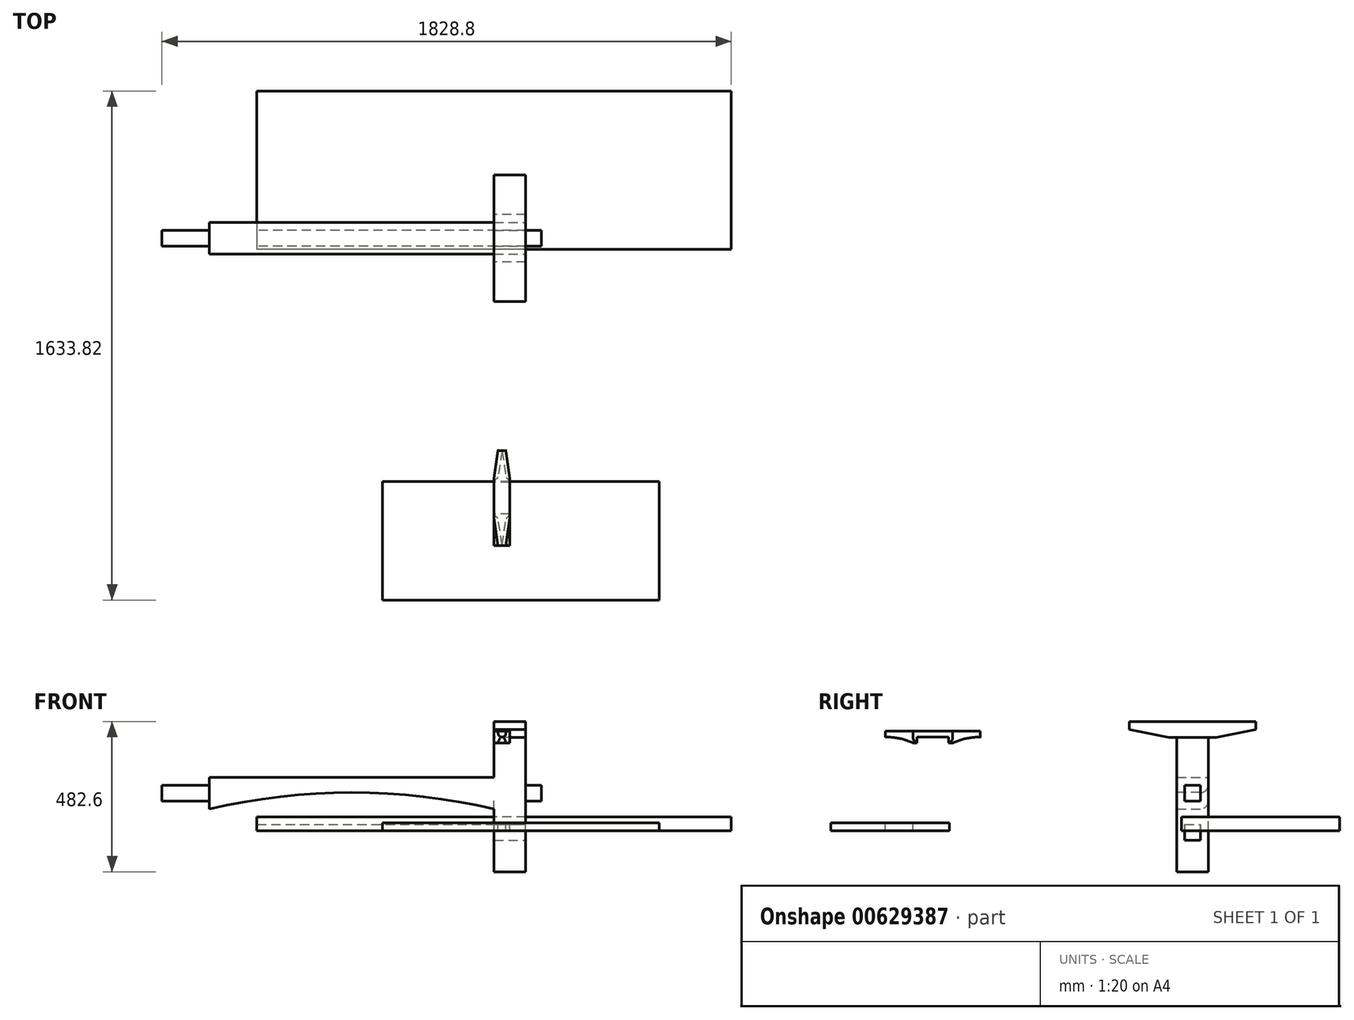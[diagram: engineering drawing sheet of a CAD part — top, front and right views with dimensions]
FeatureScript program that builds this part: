
annotation { "Feature Type Name" : "Feature", "Feature Type Description" : "" }
export const myFeature = defineFeature(function(context is Context, id is Id, definition is map)
    precondition{}
    {
        {
            var Q0;
            Q0=qCreatedBy(makeId("Top.planeOp"),FACE);
            var sketch = newSketch(context, id + "F0", { "sketchPlane" : qUnion([Q0])});
            skLineSegment(sketch, "E0.bottom", {"start": v(762, 260.88) * mm, "end": v(-762, 260.88) * mm});
            skLineSegment(sketch, "E0.top", {"start": v(762, -247.12) * mm, "end": v(-762, -247.12) * mm});
            skLineSegment(sketch, "E0.left", {"start": v(762, 260.88) * mm, "end": v(762, -247.12) * mm});
            skLineSegment(sketch, "E0.right", {"start": v(-762, 260.88) * mm, "end": v(-762, -247.12) * mm});
            skPoint(sketch, "E0.middle", {"position": v(0, 6.88) * mm});
            skSolve(sketch);
        }
        {
            var Q0;
            Q0=makeQuery(id+"F0.imprint","IMPRINT",FACE,{"disambiguationData":[TD([[makeQuery(id+"F0.imprint","IMPRINT",EDGE,{"derivedFrom":sQuery(id+"F0.wireOp",EDGE,"E0.bottom")}),1.0]])]});
            extrude(context, id + "F1", {"entities" : qUnion([Q0]), "depth" : 44.45 * mm, "offsetDistance" : 25.4 * mm});
        }
        {
            var Q0;
            Q0=qCreatedBy(makeId("Right.planeOp"),FACE);
            var sketch = newSketch(context, id + "F2", { "sketchPlane" : qUnion([Q0])});
            skLineSegment(sketch, "E1.bottom", {"start": v(-135.26, 299.84) * mm, "end": v(-287.66, 299.84) * mm});
            skLineSegment(sketch, "E1.top", {"start": v(-8.26, 350.64) * mm, "end": v(-414.66, 350.64) * mm});
            skLineSegment(sketch, "E1.left", {"start": v(-8.26, 325.24) * mm, "end": v(-8.26, 350.64) * mm});
            skLineSegment(sketch, "E1.right", {"start": v(-414.66, 325.24) * mm, "end": v(-414.66, 350.64) * mm});
            skPoint(sketch, "E1.middle", {"position": v(-211.46, 325.24) * mm});
            skLineSegment(sketch, "E2", {"start": v(-414.66, 325.24) * mm, "end": v(-287.66, 299.84) * mm});
            skLineSegment(sketch, "E3", {"start": v(-211.46, 459.59) * mm, "end": v(-211.46, 211.02) * mm, "construction": true});
            skPoint(sketch, "E3.startSnap0", {"position": v(-211.46, 350.64) * mm});
            skPoint(sketch, "E4.orphan", {"position": v(-414.66, 299.84) * mm});
            skLineSegment(sketch, "E5.MirrorCS", {"start": v(-8.26, 325.24) * mm, "end": v(-135.26, 299.84) * mm});
            skPoint(sketch, "E6.orphan", {"position": v(-8.26, 299.84) * mm});
            skSolve(sketch);
        }
        {
            var Q0;
            Q0=makeQuery(id+"F2.imprint","IMPRINT",FACE,{"disambiguationData":[TD([[makeQuery(id+"F2.imprint","IMPRINT",EDGE,{"derivedFrom":sQuery(id+"F2.wireOp",EDGE,"E1.bottom")}),-1.0]])]});
            extrude(context, id + "F3", {"entities" : qUnion([Q0]), "depth" : 101.6 * mm, "offsetDistance" : 25.4 * mm});
        }
        {
            var Q0;
            Q0=makeQuery(id+"F3.opExtrude","SWEPT_FACE",FACE,{"disambiguationData":[OSD([sQuery(id+"F2.wireOp",EDGE,"E1.bottom")])]});
            var sketch = newSketch(context, id + "F4", { "sketchPlane" : qUnion([Q0])});
            skLineSegment(sketch, "E7.bottom", {"start": v(0, 160.66) * mm, "end": v(101.6, 160.66) * mm});
            skLineSegment(sketch, "E7.top", {"start": v(0, 262.26) * mm, "end": v(101.6, 262.26) * mm});
            skLineSegment(sketch, "E7.left", {"start": v(0, 160.66) * mm, "end": v(0, 262.26) * mm});
            skLineSegment(sketch, "E7.right", {"start": v(101.6, 160.66) * mm, "end": v(101.6, 262.26) * mm});
            skPoint(sketch, "E7.middle", {"position": v(50.8, 211.46) * mm});
            skPoint(sketch, "E7.middle.positionSnap0", {"position": v(50.8, 135.26) * mm});
            skPoint(sketch, "E7.middle.positionSnap1", {"position": v(101.6, 211.46) * mm});
            skPoint(sketch, "E7.centerSnap0", {"position": v(50.8, 135.26) * mm});
            skPoint(sketch, "E7.centerSnap1", {"position": v(101.6, 211.46) * mm});
            skSolve(sketch);
        }
        {
            var Q0;
            Q0=makeQuery(id+"F4.imprint","IMPRINT",FACE,{"disambiguationData":[TD([[makeQuery(id+"F4.imprint","IMPRINT",EDGE,{"derivedFrom":sQuery(id+"F4.wireOp",EDGE,"E7.bottom")}),1.0]])]});
            extrude(context, id + "F5", {"entities" : qUnion([Q0]), "depth" : 431.8 * mm, "offsetDistance" : 25.4 * mm});
        }
        {
            var Q0;
            Q0=makeQuery(id+"F5.opExtrude","SWEPT_FACE",FACE,{"disambiguationData":[OSD([sQuery(id+"F4.wireOp",EDGE,"E7.left")])]});
            var sketch = newSketch(context, id + "F6", { "sketchPlane" : qUnion([Q0])});
            skLineSegment(sketch, "E8.bottom", {"start": v(262.26, 171.12) * mm, "end": v(160.66, 171.12) * mm});
            skLineSegment(sketch, "E8.top", {"start": v(262.26, 69.52) * mm, "end": v(160.66, 69.52) * mm});
            skLineSegment(sketch, "E8.left", {"start": v(262.26, 171.12) * mm, "end": v(262.26, 69.52) * mm});
            skLineSegment(sketch, "E8.right", {"start": v(160.66, 171.12) * mm, "end": v(160.66, 69.52) * mm});
            skPoint(sketch, "E8.middle", {"position": v(211.46, 120.32) * mm});
            skPoint(sketch, "E8.middle.positionSnap0", {"position": v(211.46, 299.84) * mm});
            skPoint(sketch, "E8.centerSnap0", {"position": v(211.46, 299.84) * mm});
            skSolve(sketch);
        }
        {
            var Q0;
            Q0=makeQuery(id+"F6.imprint","IMPRINT",FACE,{"disambiguationData":[TD([[makeQuery(id+"F6.imprint","IMPRINT",EDGE,{"derivedFrom":sQuery(id+"F6.wireOp",EDGE,"E8.bottom")}),1.0]])]});
            extrude(context, id + "F7", {"entities" : qUnion([Q0]), "depth" : 914.4 * mm, "offsetDistance" : 25.4 * mm});
        }
        {
            var Q0;
            Q0=makeQuery(id+"F7.opExtrude","CAP_FACE",FACE,{"disambiguationData":[OSD([sQuery(id+"F6.wireOp",EDGE,"E8.bottom"),sQuery(id+"F6.wireOp",EDGE,"E8.top"),sQuery(id+"F6.wireOp",EDGE,"E8.left"),sQuery(id+"F6.wireOp",EDGE,"E8.right")])],"isStart":true});
            var sketch = newSketch(context, id + "F8", { "sketchPlane" : qUnion([Q0])});
            skLineSegment(sketch, "E9.bottom", {"start": v(-186.06, 145.72) * mm, "end": v(-236.86, 145.72) * mm});
            skLineSegment(sketch, "E9.top", {"start": v(-186.06, 94.92) * mm, "end": v(-236.86, 94.92) * mm});
            skLineSegment(sketch, "E9.left", {"start": v(-186.06, 145.72) * mm, "end": v(-186.06, 94.92) * mm});
            skLineSegment(sketch, "E9.right", {"start": v(-236.86, 145.72) * mm, "end": v(-236.86, 94.92) * mm});
            skPoint(sketch, "E9.middle", {"position": v(-211.46, 120.32) * mm});
            skPoint(sketch, "E9.middle.positionSnap0", {"position": v(-262.26, 120.32) * mm});
            skPoint(sketch, "E9.middle.positionSnap1", {"position": v(-211.46, 171.12) * mm});
            skPoint(sketch, "E9.centerSnap0", {"position": v(-262.26, 120.32) * mm});
            skPoint(sketch, "E9.centerSnap1", {"position": v(-211.46, 171.12) * mm});
            skSolve(sketch);
        }
        {
            var Q0;
            Q0=makeQuery(id+"F8.imprint","IMPRINT",FACE,{"disambiguationData":[TD([[makeQuery(id+"F8.imprint","IMPRINT",EDGE,{"derivedFrom":sQuery(id+"F8.wireOp",EDGE,"E9.bottom")}),1.0]])]});
            extrude(context, id + "F9", {"entities" : qUnion([Q0]), "operationType" : NewBodyOperationType.ADD, "depth" : 152.4 * mm, "offsetDistance" : 25.4 * mm});
        }
        {
            var Q0;
            Q0=makeQuery(id+"F5.opExtrude","SWEPT_FACE",FACE,{"disambiguationData":[OSD([sQuery(id+"F4.wireOp",EDGE,"E7.right")])]});
            var sketch = newSketch(context, id + "F10", { "sketchPlane" : qUnion([Q0])});
            skLineSegment(sketch, "E10.bottom", {"start": v(-186.06, -30.36) * mm, "end": v(-236.86, -30.36) * mm});
            skLineSegment(sketch, "E10.top", {"start": v(-186.06, 20.44) * mm, "end": v(-236.86, 20.44) * mm});
            skLineSegment(sketch, "E10.left", {"start": v(-186.06, -30.36) * mm, "end": v(-186.06, 20.44) * mm});
            skLineSegment(sketch, "E10.right", {"start": v(-236.86, -30.36) * mm, "end": v(-236.86, 20.44) * mm});
            skPoint(sketch, "E10.middle", {"position": v(-211.46, -4.96) * mm});
            skPoint(sketch, "E10.middle.positionSnap0", {"position": v(-211.46, -131.96) * mm});
            skPoint(sketch, "E10.centerSnap0", {"position": v(-211.46, -131.96) * mm});
            skSolve(sketch);
        }
        {
            var Q0;
            Q0=makeQuery(id+"F10.imprint","IMPRINT",FACE,{"disambiguationData":[TD([[makeQuery(id+"F10.imprint","IMPRINT",EDGE,{"derivedFrom":sQuery(id+"F10.wireOp",EDGE,"E10.bottom")}),-1.0]])]});
            extrude(context, id + "F11", {"entities" : qUnion([Q0]), "operationType" : NewBodyOperationType.REMOVE, "endBound" : BoundingType.THROUGH_ALL, "oppositeDirection" : true, "depth" : 25.4 * mm, "offsetDistance" : 25.4 * mm});
        }
        {
            var Q0;
            Q0=makeQuery(id+"F7.opExtrude","CAP_FACE",FACE,{"disambiguationData":[OSD([sQuery(id+"F6.wireOp",EDGE,"E8.bottom"),sQuery(id+"F6.wireOp",EDGE,"E8.top"),sQuery(id+"F6.wireOp",EDGE,"E8.left"),sQuery(id+"F6.wireOp",EDGE,"E8.right")])],"isStart":false});
            var sketch = newSketch(context, id + "F12", { "sketchPlane" : qUnion([Q0])});
            skLineSegment(sketch, "E11.bottom", {"start": v(236.86, 145.72) * mm, "end": v(186.06, 145.72) * mm});
            skLineSegment(sketch, "E11.top", {"start": v(236.86, 94.92) * mm, "end": v(186.06, 94.92) * mm});
            skLineSegment(sketch, "E11.left", {"start": v(236.86, 145.72) * mm, "end": v(236.86, 94.92) * mm});
            skLineSegment(sketch, "E11.right", {"start": v(186.06, 145.72) * mm, "end": v(186.06, 94.92) * mm});
            skPoint(sketch, "E11.middle", {"position": v(211.46, 120.32) * mm});
            skPoint(sketch, "E11.middle.positionSnap0", {"position": v(262.26, 120.32) * mm});
            skPoint(sketch, "E11.middle.positionSnap1", {"position": v(211.46, 171.12) * mm});
            skPoint(sketch, "E11.centerSnap0", {"position": v(262.26, 120.32) * mm});
            skPoint(sketch, "E11.centerSnap1", {"position": v(211.46, 171.12) * mm});
            skSolve(sketch);
        }
        {
            var Q0;
            Q0=makeQuery(id+"F12.imprint","IMPRINT",FACE,{"disambiguationData":[TD([[makeQuery(id+"F12.imprint","IMPRINT",EDGE,{"derivedFrom":sQuery(id+"F12.wireOp",EDGE,"E11.bottom")}),1.0]])]});
            extrude(context, id + "F13", {"entities" : qUnion([Q0]), "operationType" : NewBodyOperationType.ADD, "depth" : 152.4 * mm, "offsetDistance" : 25.4 * mm});
        }
        {
            var Q0;
            Q0=qCreatedBy(makeId("Top.planeOp"),FACE);
            var sketch = newSketch(context, id + "F14", { "sketchPlane" : qUnion([Q0])});
            skLineSegment(sketch, "E12.bottom", {"start": v(530.86, -1372.94) * mm, "end": v(-358.14, -1372.94) * mm});
            skLineSegment(sketch, "E12.top", {"start": v(530.86, -991.94) * mm, "end": v(-358.14, -991.94) * mm});
            skLineSegment(sketch, "E12.left", {"start": v(530.86, -1372.94) * mm, "end": v(530.86, -991.94) * mm});
            skLineSegment(sketch, "E12.right", {"start": v(-358.14, -1372.94) * mm, "end": v(-358.14, -991.94) * mm});
            skPoint(sketch, "E12.middle", {"position": v(86.36, -1182.44) * mm});
            skSolve(sketch);
        }
        {
            var Q0;
            Q0=makeQuery(id+"F14.imprint","IMPRINT",FACE,{"disambiguationData":[TD([[makeQuery(id+"F14.imprint","IMPRINT",EDGE,{"derivedFrom":sQuery(id+"F14.wireOp",EDGE,"E12.bottom")}),-1.0]])]});
            extrude(context, id + "F15", {"entities" : qUnion([Q0]), "depth" : 25.4 * mm, "offsetDistance" : 25.4 * mm});
        }
        {
            var Q0;
            Q0=makeQuery(id+"F7.opExtrude","SWEPT_FACE",FACE,{"disambiguationData":[OSD([sQuery(id+"F6.wireOp",EDGE,"E8.left")])]});
            var sketch = newSketch(context, id + "F16", { "sketchPlane" : qUnion([Q0])});
            skArc(sketch, "E13", {"start": v(0, 69.52) * mm, "mid": v(-457.2, 122.3) * mm, "end": v(-914.4, 69.52) * mm});
            skSolve(sketch);
        }
        {
            var Q0;
            Q0=makeQuery(id+"F16.imprint","IMPRINT",FACE,{"disambiguationData":[TD([[makeQuery(id+"F16.imprint","IMPRINT",EDGE,{"derivedFrom":sQuery(id+"F16.wireOp",EDGE,"E13")}),1.0]])]});
            extrude(context, id + "F17", {"entities" : qUnion([Q0]), "operationType" : NewBodyOperationType.REMOVE, "endBound" : BoundingType.THROUGH_ALL, "oppositeDirection" : true, "depth" : 25.4 * mm, "offsetDistance" : 25.4 * mm});
        }
        {
            var Q0;
            Q0=qCreatedBy(makeId("Right.planeOp"),FACE);
            var sketch = newSketch(context, id + "F18", { "sketchPlane" : qUnion([Q0])});
            skLineSegment(sketch, "E14.bottom", {"start": v(-981.8, 281.46) * mm, "end": v(-994.5, 281.46) * mm});
            skLineSegment(sketch, "E14.top", {"start": v(-892.9, 319.56) * mm, "end": v(-1197.7, 319.56) * mm});
            skLineSegment(sketch, "E14.left", {"start": v(-892.9, 300.51) * mm, "end": v(-892.9, 319.56) * mm});
            skLineSegment(sketch, "E14.right", {"start": v(-1197.7, 300.51) * mm, "end": v(-1197.7, 319.56) * mm});
            skPoint(sketch, "E14.middle", {"position": v(-1045.3, 300.51) * mm});
            skPoint(sketch, "E15.orphan", {"position": v(-1197.7, 281.46) * mm});
            skLineSegment(sketch, "E16", {"start": v(-1045.3, 344.35) * mm, "end": v(-1045.3, 234.3) * mm, "construction": true});
            skPoint(sketch, "E17.orphan", {"position": v(-892.9, 281.46) * mm});
            skLineSegment(sketch, "E18.top", {"start": v(-994.5, 300.51) * mm, "end": v(-1096.1, 300.51) * mm});
            skLineSegment(sketch, "E18.left", {"start": v(-994.5, 281.46) * mm, "end": v(-994.5, 300.51) * mm});
            skLineSegment(sketch, "E18.right", {"start": v(-1096.1, 281.46) * mm, "end": v(-1096.1, 300.51) * mm});
            skPoint(sketch, "E18.middle", {"position": v(-1045.3, 281.46) * mm});
            skLineSegment(sketch, "E19.trimOffspring", {"start": v(-1096.1, 281.46) * mm, "end": v(-1108.8, 281.46) * mm});
            skArc(sketch, "E20", {"start": v(-1108.8, 281.46) * mm, "mid": v(-1152.15, 296.1) * mm, "end": v(-1197.7, 300.51) * mm});
            skArc(sketch, "E21.MirrorCS", {"start": v(-981.8, 281.46) * mm, "mid": v(-938.44, 296.1) * mm, "end": v(-892.9, 300.51) * mm});
            skSolve(sketch);
        }
        {
            var Q0;
            Q0=makeQuery(id+"F18.imprint","IMPRINT",FACE,{"disambiguationData":[TD([[makeQuery(id+"F18.imprint","IMPRINT",EDGE,{"derivedFrom":sQuery(id+"F18.wireOp",EDGE,"E14.bottom")}),-1.0]])]});
            extrude(context, id + "F19", {"entities" : qUnion([Q0]), "depth" : 50.8 * mm, "offsetDistance" : 25.4 * mm});
        }
        {
            var Q0;
            Q0=makeQuery(id+"F19.opExtrude","SWEPT_FACE",FACE,{"disambiguationData":[OSD([sQuery(id+"F18.wireOp",EDGE,"E14.top")])]});
            var sketch = newSketch(context, id + "F20", { "sketchPlane" : qUnion([Q0])});
            skLineSegment(sketch, "E22.bottom", {"start": v(38.1, -1108.8) * mm, "end": v(12.7, -1108.8) * mm});
            skLineSegment(sketch, "E22.top", {"start": v(38.1, -1286.6) * mm, "end": v(12.7, -1286.6) * mm});
            skLineSegment(sketch, "E22.left", {"start": v(38.1, -1108.8) * mm, "end": v(38.1, -1286.6) * mm});
            skLineSegment(sketch, "E22.right", {"start": v(12.7, -1108.8) * mm, "end": v(12.7, -1286.6) * mm});
            skPoint(sketch, "E22.middle", {"position": v(25.4, -1197.7) * mm});
            skLineSegment(sketch, "E23", {"start": v(38.1, -1197.7) * mm, "end": v(50.8, -1108.8) * mm});
            skLineSegment(sketch, "E24", {"start": v(12.7, -1197.7) * mm, "end": v(0, -1108.8) * mm});
            skLineSegment(sketch, "E25", {"start": v(0, -1045.3) * mm, "end": v(115.07, -1045.3) * mm, "construction": true});
            skLineSegment(sketch, "E26.MirrorCS", {"start": v(38.1, -892.9) * mm, "end": v(50.8, -981.8) * mm});
            skLineSegment(sketch, "E27.MirrorCS", {"start": v(12.7, -892.9) * mm, "end": v(0, -981.8) * mm});
            skSolve(sketch);
        }
        {
            var Q0;
            {var subQ0=sQuery(id+"F20.wireOp",EDGE,"E26.MirrorCS");Q0=makeQuery(id+"F20.imprint","IMPRINT",FACE,{"disambiguationData":[TD([[makeQuery(id+"F20.imprint","IMPRINT",EDGE,{"derivedFrom":subQ0}),1.0]])]});}
            var Q1;
            {var subQ0=sQuery(id+"F20.wireOp",EDGE,"E27.MirrorCS");Q1=makeQuery(id+"F20.imprint","IMPRINT",FACE,{"disambiguationData":[TD([[makeQuery(id+"F20.imprint","IMPRINT",EDGE,{"derivedFrom":subQ0}),-1.0]])]});}
            var Q2;
            {var subQ0=sQuery(id+"F20.wireOp",EDGE,"E24");Q2=makeQuery(id+"F20.imprint","IMPRINT",FACE,{"disambiguationData":[TD([[makeQuery(id+"F20.imprint","IMPRINT",EDGE,{"derivedFrom":subQ0}),1.0]])]});}
            var Q3;
            {var subQ0=sQuery(id+"F20.wireOp",EDGE,"E23");Q3=makeQuery(id+"F20.imprint","IMPRINT",FACE,{"disambiguationData":[TD([[makeQuery(id+"F20.imprint","IMPRINT",EDGE,{"derivedFrom":subQ0}),-1.0]])]});}
            extrude(context, id + "F21", {"entities" : qUnion([Q0, Q1, Q2, Q3]), "operationType" : NewBodyOperationType.REMOVE, "endBound" : BoundingType.THROUGH_ALL, "oppositeDirection" : true, "depth" : 25.4 * mm, "offsetDistance" : 25.4 * mm});
        }
        {
            var Q0;
            Q0=makeQuery(id+"F21.boolean.opBoolean","INTERSECT",EDGE,{"derivedFrom":[makeQuery(id+"F19.opExtrude","SWEPT_FACE",FACE,{"disambiguationData":[OSD([sQuery(id+"F18.wireOp",EDGE,"E20")])]}),makeQuery(id+"F21.opExtrude","SWEPT_FACE",FACE,{"disambiguationData":[OSD([sQuery(id+"F20.wireOp",EDGE,"E23")])]})]});
            var Q1;
            Q1=makeQuery(id+"F21.boolean.opBoolean","INTERSECT",EDGE,{"derivedFrom":[makeQuery(id+"F19.opExtrude","SWEPT_FACE",FACE,{"disambiguationData":[OSD([sQuery(id+"F18.wireOp",EDGE,"E20")])]}),makeQuery(id+"F21.opExtrude","SWEPT_FACE",FACE,{"disambiguationData":[OSD([sQuery(id+"F20.wireOp",EDGE,"E24")])]})]});
            var Q2;
            Q2=makeQuery(id+"F21.boolean.opBoolean","INTERSECT",EDGE,{"derivedFrom":[makeQuery(id+"F19.opExtrude","SWEPT_FACE",FACE,{"disambiguationData":[OSD([sQuery(id+"F18.wireOp",EDGE,"E21.MirrorCS")])]}),makeQuery(id+"F21.opExtrude","SWEPT_FACE",FACE,{"disambiguationData":[OSD([sQuery(id+"F20.wireOp",EDGE,"E26.MirrorCS")])]})]});
            var Q3;
            Q3=makeQuery(id+"F21.boolean.opBoolean","INTERSECT",EDGE,{"derivedFrom":[makeQuery(id+"F19.opExtrude","SWEPT_FACE",FACE,{"disambiguationData":[OSD([sQuery(id+"F18.wireOp",EDGE,"E21.MirrorCS")])]}),makeQuery(id+"F21.opExtrude","SWEPT_FACE",FACE,{"disambiguationData":[OSD([sQuery(id+"F20.wireOp",EDGE,"E27.MirrorCS")])]})]});
            var Q4;
            Q4=makeQuery(id+"F19.opExtrude","SWEPT_EDGE",EDGE,{"disambiguationData":[OSD([sQuery(id+"F18.wireOp",EDGE,"E19.trimOffspring"),sQuery(id+"F18.wireOp",EDGE,"E20")])]});
            var Q5;
            Q5=makeQuery(id+"F19.opExtrude","SWEPT_EDGE",EDGE,{"disambiguationData":[OSD([sQuery(id+"F18.wireOp",EDGE,"E14.bottom"),sQuery(id+"F18.wireOp",EDGE,"E21.MirrorCS")])]});
            fillet(context, id + "F22", {"entities" : qUnion([Q0, Q1, Q2, Q3, Q4, Q5]), "radius" : 12.7 * mm, "tangentPropagation" : true, "allowEdgeOverflow" : false});
        }
        {
            var Q0;
            Q0=makeQuery(id+"F17.boolean.opBoolean","COPY",EDGE,{"derivedFrom":makeQuery(id+"F17.opExtrude","CAP_EDGE",EDGE,{"disambiguationData":[OSD([sQuery(id+"F16.wireOp",EDGE,"E13")])],"isStart":true})});
            var Q1;
            Q1=makeQuery(id+"F17.boolean.opBoolean","INTERSECT",EDGE,{"derivedFrom":[makeQuery(id+"F7.opExtrude","SWEPT_FACE",FACE,{"disambiguationData":[OSD([sQuery(id+"F6.wireOp",EDGE,"E8.right")])]}),makeQuery(id+"F17.opExtrude","SWEPT_FACE",FACE,{"disambiguationData":[OSD([sQuery(id+"F16.wireOp",EDGE,"E13")])]})]});
            fillet(context, id + "F23", {"entities" : qUnion([Q0, Q1]), "radius" : 25.4 * mm, "tangentPropagation" : true, "allowEdgeOverflow" : false});
        }
    });
